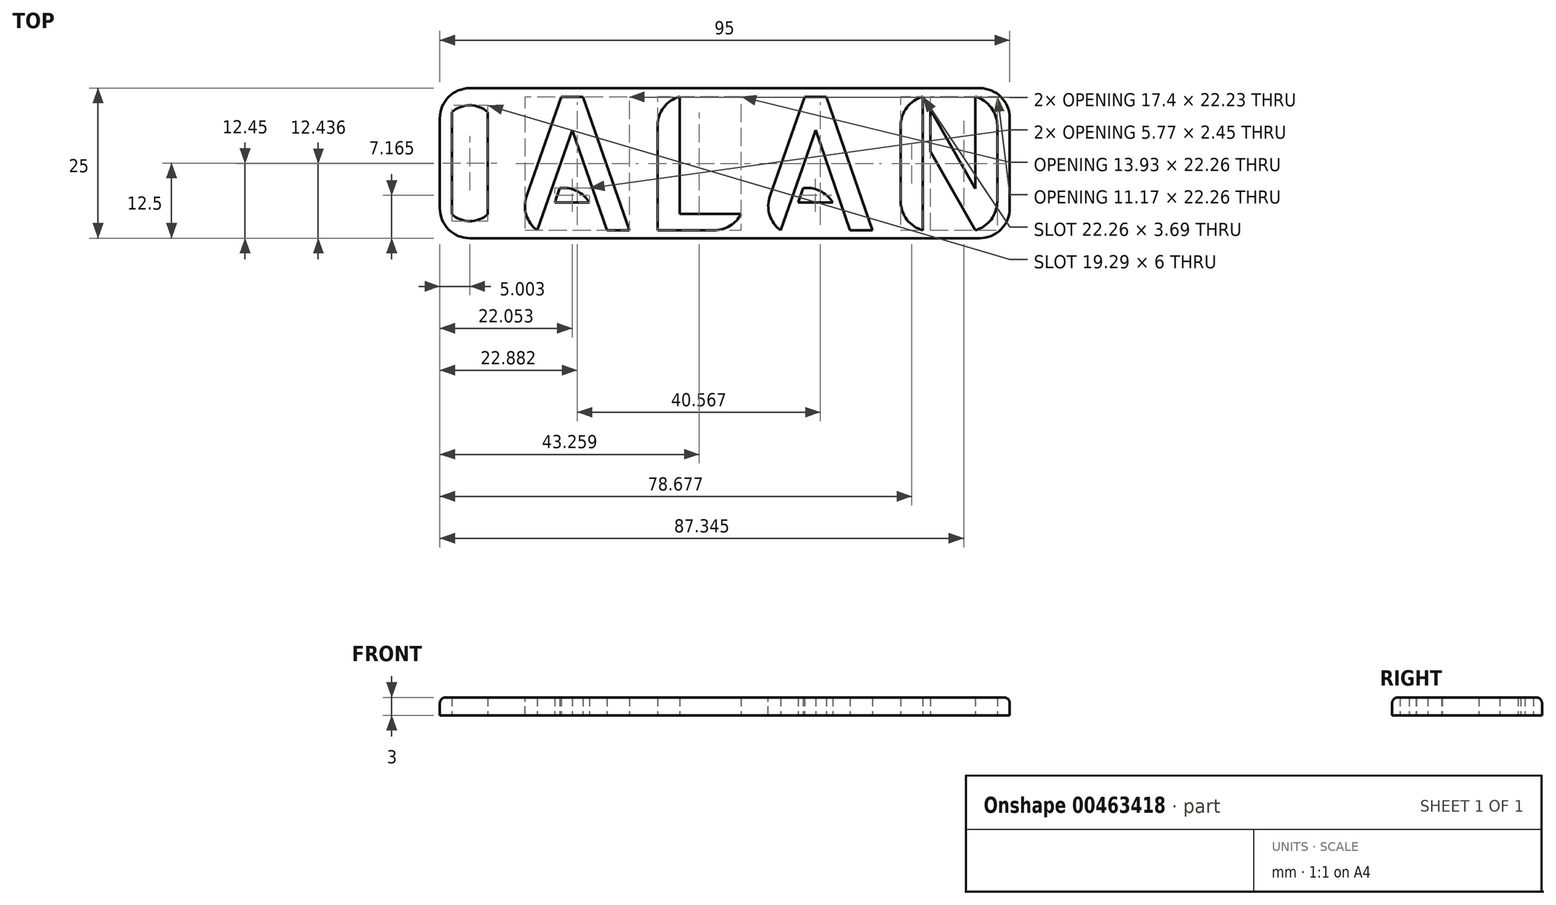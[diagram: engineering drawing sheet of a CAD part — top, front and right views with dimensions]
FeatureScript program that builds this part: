
annotation { "Feature Type Name" : "Feature", "Feature Type Description" : "" }
export const myFeature = defineFeature(function(context is Context, id is Id, definition is map)
    precondition{}
    {
        {
            var Q0;
            Q0=qCreatedBy(makeId("Top.planeOp"),FACE);
            var sketch = newSketch(context, id + "F0", { "sketchPlane" : qUnion([Q0])});
            skLineSegment(sketch, "E0.bottom", {"start": v(46.95, -25) * mm, "end": v(-48.05, -25) * mm});
            skLineSegment(sketch, "E0.top", {"start": v(46.95, 0) * mm, "end": v(-48.05, 0) * mm});
            skLineSegment(sketch, "E0.left", {"start": v(46.95, -25) * mm, "end": v(46.95, 0) * mm});
            skLineSegment(sketch, "E0.right", {"start": v(-48.05, -25) * mm, "end": v(-48.05, 0) * mm});
            skPoint(sketch, "E1.endSnap0", {"position": v(-48.05, -12.5) * mm});
            skText(sketch, "E2", { "text": "ALAN", "fontName": "AllertaStencil-Regular.ttf"});
            skArc(sketch, "E3", {"start": v(-40.05, -4) * mm, "mid": v(-43.05, -2.85) * mm, "end": v(-46.05, -4) * mm});
            skArc(sketch, "E4", {"start": v(-46.05, -21) * mm, "mid": v(-43.05, -22.15) * mm, "end": v(-40.05, -21) * mm});
            skLineSegment(sketch, "E5", {"start": v(-46.05, -4) * mm, "end": v(-46.05, -21) * mm});
            skLineSegment(sketch, "E6", {"start": v(-40.05, -4) * mm, "end": v(-40.05, -21) * mm});
            const initialGuessF0  = {"E2": [-0.03749, -0.02368, 1, 0, 0.02227]};
            skSetInitialGuess(sketch, initialGuessF0);
            skSolve(sketch);
        }
        {
            var Q0;
            Q0=makeQuery(id+"F0.imprint","IMPRINT",FACE,{"disambiguationData":[TD([[makeQuery(id+"F0.imprint","IMPRINT",EDGE,{"derivedFrom":sQuery(id+"F0.wireOp",EDGE,"E0.bottom")}),-1.0]])]});
            extrude(context, id + "F1", {"entities" : qUnion([Q0]), "depth" : 3 * mm});
        }
        {
            var Q0;
            Q0=makeQuery(id+"F1.opExtrude","SWEPT_EDGE",EDGE,{"disambiguationData":[OSD([sQuery(id+"F0.wireOp",EDGE,"E0.bottom"),sQuery(id+"F0.wireOp",EDGE,"E0.right")])]});
            var Q1;
            Q1=makeQuery(id+"F1.opExtrude","SWEPT_EDGE",EDGE,{"disambiguationData":[OSD([sQuery(id+"F0.wireOp",EDGE,"E0.top"),sQuery(id+"F0.wireOp",EDGE,"E0.right")])]});
            var Q2;
            Q2=makeQuery(id+"F1.opExtrude","SWEPT_EDGE",EDGE,{"disambiguationData":[OSD([sQuery(id+"F0.wireOp",EDGE,"E0.bottom"),sQuery(id+"F0.wireOp",EDGE,"E0.left")])]});
            var Q3;
            Q3=makeQuery(id+"F1.opExtrude","SWEPT_EDGE",EDGE,{"disambiguationData":[OSD([sQuery(id+"F0.wireOp",EDGE,"E0.top"),sQuery(id+"F0.wireOp",EDGE,"E0.left")])]});
            fillet(context, id + "F2", {"entities" : qUnion([Q0, Q1, Q2, Q3]), "radius" : 5 * mm, "tangentPropagation" : true, "allowEdgeOverflow" : false});
        }
        {
            var Q0;
            Q0=makeQuery(id+"F1.opExtrude","SWEPT_EDGE",EDGE,{"disambiguationData":[OSD([sQuery(id+"F0.wireOp",EDGE,"E2.sketch_text.stroke-28"),sQuery(id+"F0.wireOp",EDGE,"E2.sketch_text.stroke-29")])]});
            var Q1;
            Q1=makeQuery(id+"F1.opExtrude","SWEPT_EDGE",EDGE,{"disambiguationData":[OSD([sQuery(id+"F0.wireOp",EDGE,"E2.sketch_text.stroke-35"),sQuery(id+"F0.wireOp",EDGE,"E2.sketch_text.stroke-38")])]});
            var Q2;
            Q2=makeQuery(id+"F1.opExtrude","SWEPT_EDGE",EDGE,{"disambiguationData":[OSD([sQuery(id+"F0.wireOp",EDGE,"E2.sketch_text.stroke-35"),sQuery(id+"F0.wireOp",EDGE,"E2.sketch_text.stroke-36")])]});
            var Q3;
            Q3=makeQuery(id+"F1.opExtrude","SWEPT_EDGE",EDGE,{"disambiguationData":[OSD([sQuery(id+"F0.wireOp",EDGE,"E2.sketch_text.stroke-29"),sQuery(id+"F0.wireOp",EDGE,"E2.sketch_text.stroke-30")])]});
            var Q4;
            Q4=makeQuery(id+"F1.opExtrude","SWEPT_EDGE",EDGE,{"disambiguationData":[OSD([sQuery(id+"F0.wireOp",EDGE,"E2.sketch_text.stroke-20"),sQuery(id+"F0.wireOp",EDGE,"E2.sketch_text.stroke-21")])]});
            var Q5;
            Q5=makeQuery(id+"F1.opExtrude","SWEPT_EDGE",EDGE,{"disambiguationData":[OSD([sQuery(id+"F0.wireOp",EDGE,"E2.sketch_text.stroke-13"),sQuery(id+"F0.wireOp",EDGE,"E2.sketch_text.stroke-14")])]});
            var Q6;
            Q6=makeQuery(id+"F1.opExtrude","SWEPT_EDGE",EDGE,{"disambiguationData":[OSD([sQuery(id+"F0.wireOp",EDGE,"E2.sketch_text.stroke-15"),sQuery(id+"F0.wireOp",EDGE,"E2.sketch_text.stroke-16")])]});
            var Q7;
            Q7=makeQuery(id+"F1.opExtrude","SWEPT_EDGE",EDGE,{"disambiguationData":[OSD([sQuery(id+"F0.wireOp",EDGE,"E2.sketch_text.stroke-3"),sQuery(id+"F0.wireOp",EDGE,"E2.sketch_text.stroke-4")])]});
            var Q8;
            Q8=makeQuery(id+"F1.opExtrude","SWEPT_EDGE",EDGE,{"disambiguationData":[OSD([sQuery(id+"F0.wireOp",EDGE,"E2.sketch_text.stroke-7"),sQuery(id+"F0.wireOp",EDGE,"E2.sketch_text.stroke-10")])]});
            var Q9;
            Q9=makeQuery(id+"F1.opExtrude","SWEPT_EDGE",EDGE,{"disambiguationData":[OSD([sQuery(id+"F0.wireOp",EDGE,"E2.sketch_text.stroke-24"),sQuery(id+"F0.wireOp",EDGE,"E2.sketch_text.stroke-27")])]});
            fillet(context, id + "F3", {"entities" : qUnion([Q0, Q1, Q2, Q3, Q4, Q5, Q6, Q7, Q8, Q9]), "radius" : 5 * mm, "tangentPropagation" : true, "allowEdgeOverflow" : false});
        }
        {
            var Q0;
            Q0=makeQuery(id+"F1.opExtrude","CAP_EDGE",EDGE,{"disambiguationData":[OSD([sQuery(id+"F0.wireOp",EDGE,"E0.top")])],"isStart":false});
            var Q1;
            {var subQ0=sQuery(id+"F0.wireOp",EDGE,"E0.right");var subQ1=sQuery(id+"F0.wireOp",EDGE,"E0.top");Q1=makeQuery(id+"F2.opFillet","BLEND_EDGE",EDGE,{"blendedFrom":[makeQuery(id+"F1.opExtrude","SWEPT_EDGE",EDGE,{"disambiguationData":[OSD([subQ1,subQ0])]}),makeQuery(id+"F1.opExtrude","CAP_FACE",FACE,{"disambiguationData":[OSD([sQuery(id+"F0.wireOp",EDGE,"E0.bottom"),subQ1,sQuery(id+"F0.wireOp",EDGE,"E0.left"),subQ0,sQuery(id+"F0.wireOp",EDGE,"E2.sketch_text.stroke-0"),sQuery(id+"F0.wireOp",EDGE,"E2.sketch_text.stroke-1"),sQuery(id+"F0.wireOp",EDGE,"E2.sketch_text.stroke-2"),sQuery(id+"F0.wireOp",EDGE,"E2.sketch_text.stroke-3"),sQuery(id+"F0.wireOp",EDGE,"E2.sketch_text.stroke-4"),sQuery(id+"F0.wireOp",EDGE,"E2.sketch_text.stroke-5"),sQuery(id+"F0.wireOp",EDGE,"E2.sketch_text.stroke-6"),sQuery(id+"F0.wireOp",EDGE,"E2.sketch_text.stroke-7"),sQuery(id+"F0.wireOp",EDGE,"E2.sketch_text.stroke-8"),sQuery(id+"F0.wireOp",EDGE,"E2.sketch_text.stroke-9"),sQuery(id+"F0.wireOp",EDGE,"E2.sketch_text.stroke-10"),sQuery(id+"F0.wireOp",EDGE,"E2.sketch_text.stroke-11"),sQuery(id+"F0.wireOp",EDGE,"E2.sketch_text.stroke-12"),sQuery(id+"F0.wireOp",EDGE,"E2.sketch_text.stroke-13"),sQuery(id+"F0.wireOp",EDGE,"E2.sketch_text.stroke-14"),sQuery(id+"F0.wireOp",EDGE,"E2.sketch_text.stroke-15"),sQuery(id+"F0.wireOp",EDGE,"E2.sketch_text.stroke-16"),sQuery(id+"F0.wireOp",EDGE,"E2.sketch_text.stroke-17"),sQuery(id+"F0.wireOp",EDGE,"E2.sketch_text.stroke-18"),sQuery(id+"F0.wireOp",EDGE,"E2.sketch_text.stroke-19"),sQuery(id+"F0.wireOp",EDGE,"E2.sketch_text.stroke-20"),sQuery(id+"F0.wireOp",EDGE,"E2.sketch_text.stroke-21"),sQuery(id+"F0.wireOp",EDGE,"E2.sketch_text.stroke-22"),sQuery(id+"F0.wireOp",EDGE,"E2.sketch_text.stroke-23"),sQuery(id+"F0.wireOp",EDGE,"E2.sketch_text.stroke-24"),sQuery(id+"F0.wireOp",EDGE,"E2.sketch_text.stroke-25"),sQuery(id+"F0.wireOp",EDGE,"E2.sketch_text.stroke-26"),sQuery(id+"F0.wireOp",EDGE,"E2.sketch_text.stroke-27"),sQuery(id+"F0.wireOp",EDGE,"E2.sketch_text.stroke-28"),sQuery(id+"F0.wireOp",EDGE,"E2.sketch_text.stroke-29"),sQuery(id+"F0.wireOp",EDGE,"E2.sketch_text.stroke-30"),sQuery(id+"F0.wireOp",EDGE,"E2.sketch_text.stroke-31"),sQuery(id+"F0.wireOp",EDGE,"E2.sketch_text.stroke-32"),sQuery(id+"F0.wireOp",EDGE,"E2.sketch_text.stroke-33"),sQuery(id+"F0.wireOp",EDGE,"E2.sketch_text.stroke-34"),sQuery(id+"F0.wireOp",EDGE,"E2.sketch_text.stroke-35"),sQuery(id+"F0.wireOp",EDGE,"E2.sketch_text.stroke-36"),sQuery(id+"F0.wireOp",EDGE,"E2.sketch_text.stroke-37"),sQuery(id+"F0.wireOp",EDGE,"E2.sketch_text.stroke-38"),sQuery(id+"F0.wireOp",EDGE,"E3"),sQuery(id+"F0.wireOp",EDGE,"E4"),sQuery(id+"F0.wireOp",EDGE,"E5"),sQuery(id+"F0.wireOp",EDGE,"E6")])],"isStart":false})],"blendedInto":[makeQuery(id+"F1.opExtrude","CAP_FACE",FACE,{"disambiguationData":[OSD([sQuery(id+"F0.wireOp",EDGE,"E0.bottom"),subQ1,sQuery(id+"F0.wireOp",EDGE,"E0.left"),subQ0,sQuery(id+"F0.wireOp",EDGE,"E2.sketch_text.stroke-0"),sQuery(id+"F0.wireOp",EDGE,"E2.sketch_text.stroke-1"),sQuery(id+"F0.wireOp",EDGE,"E2.sketch_text.stroke-2"),sQuery(id+"F0.wireOp",EDGE,"E2.sketch_text.stroke-3"),sQuery(id+"F0.wireOp",EDGE,"E2.sketch_text.stroke-4"),sQuery(id+"F0.wireOp",EDGE,"E2.sketch_text.stroke-5"),sQuery(id+"F0.wireOp",EDGE,"E2.sketch_text.stroke-6"),sQuery(id+"F0.wireOp",EDGE,"E2.sketch_text.stroke-7"),sQuery(id+"F0.wireOp",EDGE,"E2.sketch_text.stroke-8"),sQuery(id+"F0.wireOp",EDGE,"E2.sketch_text.stroke-9"),sQuery(id+"F0.wireOp",EDGE,"E2.sketch_text.stroke-10"),sQuery(id+"F0.wireOp",EDGE,"E2.sketch_text.stroke-11"),sQuery(id+"F0.wireOp",EDGE,"E2.sketch_text.stroke-12"),sQuery(id+"F0.wireOp",EDGE,"E2.sketch_text.stroke-13"),sQuery(id+"F0.wireOp",EDGE,"E2.sketch_text.stroke-14"),sQuery(id+"F0.wireOp",EDGE,"E2.sketch_text.stroke-15"),sQuery(id+"F0.wireOp",EDGE,"E2.sketch_text.stroke-16"),sQuery(id+"F0.wireOp",EDGE,"E2.sketch_text.stroke-17"),sQuery(id+"F0.wireOp",EDGE,"E2.sketch_text.stroke-18"),sQuery(id+"F0.wireOp",EDGE,"E2.sketch_text.stroke-19"),sQuery(id+"F0.wireOp",EDGE,"E2.sketch_text.stroke-20"),sQuery(id+"F0.wireOp",EDGE,"E2.sketch_text.stroke-21"),sQuery(id+"F0.wireOp",EDGE,"E2.sketch_text.stroke-22"),sQuery(id+"F0.wireOp",EDGE,"E2.sketch_text.stroke-23"),sQuery(id+"F0.wireOp",EDGE,"E2.sketch_text.stroke-24"),sQuery(id+"F0.wireOp",EDGE,"E2.sketch_text.stroke-25"),sQuery(id+"F0.wireOp",EDGE,"E2.sketch_text.stroke-26"),sQuery(id+"F0.wireOp",EDGE,"E2.sketch_text.stroke-27"),sQuery(id+"F0.wireOp",EDGE,"E2.sketch_text.stroke-28"),sQuery(id+"F0.wireOp",EDGE,"E2.sketch_text.stroke-29"),sQuery(id+"F0.wireOp",EDGE,"E2.sketch_text.stroke-30"),sQuery(id+"F0.wireOp",EDGE,"E2.sketch_text.stroke-31"),sQuery(id+"F0.wireOp",EDGE,"E2.sketch_text.stroke-32"),sQuery(id+"F0.wireOp",EDGE,"E2.sketch_text.stroke-33"),sQuery(id+"F0.wireOp",EDGE,"E2.sketch_text.stroke-34"),sQuery(id+"F0.wireOp",EDGE,"E2.sketch_text.stroke-35"),sQuery(id+"F0.wireOp",EDGE,"E2.sketch_text.stroke-36"),sQuery(id+"F0.wireOp",EDGE,"E2.sketch_text.stroke-37"),sQuery(id+"F0.wireOp",EDGE,"E2.sketch_text.stroke-38"),sQuery(id+"F0.wireOp",EDGE,"E3"),sQuery(id+"F0.wireOp",EDGE,"E4"),sQuery(id+"F0.wireOp",EDGE,"E5"),sQuery(id+"F0.wireOp",EDGE,"E6")])],"isStart":false})]});}
            var Q2;
            Q2=makeQuery(id+"F1.opExtrude","CAP_EDGE",EDGE,{"disambiguationData":[OSD([sQuery(id+"F0.wireOp",EDGE,"E0.right")])],"isStart":false});
            var Q3;
            {var subQ0=sQuery(id+"F0.wireOp",EDGE,"E0.right");var subQ1=sQuery(id+"F0.wireOp",EDGE,"E0.bottom");Q3=makeQuery(id+"F2.opFillet","BLEND_EDGE",EDGE,{"blendedFrom":[makeQuery(id+"F1.opExtrude","SWEPT_EDGE",EDGE,{"disambiguationData":[OSD([subQ1,subQ0])]}),makeQuery(id+"F1.opExtrude","CAP_FACE",FACE,{"disambiguationData":[OSD([subQ1,sQuery(id+"F0.wireOp",EDGE,"E0.top"),sQuery(id+"F0.wireOp",EDGE,"E0.left"),subQ0,sQuery(id+"F0.wireOp",EDGE,"E2.sketch_text.stroke-0"),sQuery(id+"F0.wireOp",EDGE,"E2.sketch_text.stroke-1"),sQuery(id+"F0.wireOp",EDGE,"E2.sketch_text.stroke-2"),sQuery(id+"F0.wireOp",EDGE,"E2.sketch_text.stroke-3"),sQuery(id+"F0.wireOp",EDGE,"E2.sketch_text.stroke-4"),sQuery(id+"F0.wireOp",EDGE,"E2.sketch_text.stroke-5"),sQuery(id+"F0.wireOp",EDGE,"E2.sketch_text.stroke-6"),sQuery(id+"F0.wireOp",EDGE,"E2.sketch_text.stroke-7"),sQuery(id+"F0.wireOp",EDGE,"E2.sketch_text.stroke-8"),sQuery(id+"F0.wireOp",EDGE,"E2.sketch_text.stroke-9"),sQuery(id+"F0.wireOp",EDGE,"E2.sketch_text.stroke-10"),sQuery(id+"F0.wireOp",EDGE,"E2.sketch_text.stroke-11"),sQuery(id+"F0.wireOp",EDGE,"E2.sketch_text.stroke-12"),sQuery(id+"F0.wireOp",EDGE,"E2.sketch_text.stroke-13"),sQuery(id+"F0.wireOp",EDGE,"E2.sketch_text.stroke-14"),sQuery(id+"F0.wireOp",EDGE,"E2.sketch_text.stroke-15"),sQuery(id+"F0.wireOp",EDGE,"E2.sketch_text.stroke-16"),sQuery(id+"F0.wireOp",EDGE,"E2.sketch_text.stroke-17"),sQuery(id+"F0.wireOp",EDGE,"E2.sketch_text.stroke-18"),sQuery(id+"F0.wireOp",EDGE,"E2.sketch_text.stroke-19"),sQuery(id+"F0.wireOp",EDGE,"E2.sketch_text.stroke-20"),sQuery(id+"F0.wireOp",EDGE,"E2.sketch_text.stroke-21"),sQuery(id+"F0.wireOp",EDGE,"E2.sketch_text.stroke-22"),sQuery(id+"F0.wireOp",EDGE,"E2.sketch_text.stroke-23"),sQuery(id+"F0.wireOp",EDGE,"E2.sketch_text.stroke-24"),sQuery(id+"F0.wireOp",EDGE,"E2.sketch_text.stroke-25"),sQuery(id+"F0.wireOp",EDGE,"E2.sketch_text.stroke-26"),sQuery(id+"F0.wireOp",EDGE,"E2.sketch_text.stroke-27"),sQuery(id+"F0.wireOp",EDGE,"E2.sketch_text.stroke-28"),sQuery(id+"F0.wireOp",EDGE,"E2.sketch_text.stroke-29"),sQuery(id+"F0.wireOp",EDGE,"E2.sketch_text.stroke-30"),sQuery(id+"F0.wireOp",EDGE,"E2.sketch_text.stroke-31"),sQuery(id+"F0.wireOp",EDGE,"E2.sketch_text.stroke-32"),sQuery(id+"F0.wireOp",EDGE,"E2.sketch_text.stroke-33"),sQuery(id+"F0.wireOp",EDGE,"E2.sketch_text.stroke-34"),sQuery(id+"F0.wireOp",EDGE,"E2.sketch_text.stroke-35"),sQuery(id+"F0.wireOp",EDGE,"E2.sketch_text.stroke-36"),sQuery(id+"F0.wireOp",EDGE,"E2.sketch_text.stroke-37"),sQuery(id+"F0.wireOp",EDGE,"E2.sketch_text.stroke-38"),sQuery(id+"F0.wireOp",EDGE,"E3"),sQuery(id+"F0.wireOp",EDGE,"E4"),sQuery(id+"F0.wireOp",EDGE,"E5"),sQuery(id+"F0.wireOp",EDGE,"E6")])],"isStart":false})],"blendedInto":[makeQuery(id+"F1.opExtrude","CAP_FACE",FACE,{"disambiguationData":[OSD([subQ1,sQuery(id+"F0.wireOp",EDGE,"E0.top"),sQuery(id+"F0.wireOp",EDGE,"E0.left"),subQ0,sQuery(id+"F0.wireOp",EDGE,"E2.sketch_text.stroke-0"),sQuery(id+"F0.wireOp",EDGE,"E2.sketch_text.stroke-1"),sQuery(id+"F0.wireOp",EDGE,"E2.sketch_text.stroke-2"),sQuery(id+"F0.wireOp",EDGE,"E2.sketch_text.stroke-3"),sQuery(id+"F0.wireOp",EDGE,"E2.sketch_text.stroke-4"),sQuery(id+"F0.wireOp",EDGE,"E2.sketch_text.stroke-5"),sQuery(id+"F0.wireOp",EDGE,"E2.sketch_text.stroke-6"),sQuery(id+"F0.wireOp",EDGE,"E2.sketch_text.stroke-7"),sQuery(id+"F0.wireOp",EDGE,"E2.sketch_text.stroke-8"),sQuery(id+"F0.wireOp",EDGE,"E2.sketch_text.stroke-9"),sQuery(id+"F0.wireOp",EDGE,"E2.sketch_text.stroke-10"),sQuery(id+"F0.wireOp",EDGE,"E2.sketch_text.stroke-11"),sQuery(id+"F0.wireOp",EDGE,"E2.sketch_text.stroke-12"),sQuery(id+"F0.wireOp",EDGE,"E2.sketch_text.stroke-13"),sQuery(id+"F0.wireOp",EDGE,"E2.sketch_text.stroke-14"),sQuery(id+"F0.wireOp",EDGE,"E2.sketch_text.stroke-15"),sQuery(id+"F0.wireOp",EDGE,"E2.sketch_text.stroke-16"),sQuery(id+"F0.wireOp",EDGE,"E2.sketch_text.stroke-17"),sQuery(id+"F0.wireOp",EDGE,"E2.sketch_text.stroke-18"),sQuery(id+"F0.wireOp",EDGE,"E2.sketch_text.stroke-19"),sQuery(id+"F0.wireOp",EDGE,"E2.sketch_text.stroke-20"),sQuery(id+"F0.wireOp",EDGE,"E2.sketch_text.stroke-21"),sQuery(id+"F0.wireOp",EDGE,"E2.sketch_text.stroke-22"),sQuery(id+"F0.wireOp",EDGE,"E2.sketch_text.stroke-23"),sQuery(id+"F0.wireOp",EDGE,"E2.sketch_text.stroke-24"),sQuery(id+"F0.wireOp",EDGE,"E2.sketch_text.stroke-25"),sQuery(id+"F0.wireOp",EDGE,"E2.sketch_text.stroke-26"),sQuery(id+"F0.wireOp",EDGE,"E2.sketch_text.stroke-27"),sQuery(id+"F0.wireOp",EDGE,"E2.sketch_text.stroke-28"),sQuery(id+"F0.wireOp",EDGE,"E2.sketch_text.stroke-29"),sQuery(id+"F0.wireOp",EDGE,"E2.sketch_text.stroke-30"),sQuery(id+"F0.wireOp",EDGE,"E2.sketch_text.stroke-31"),sQuery(id+"F0.wireOp",EDGE,"E2.sketch_text.stroke-32"),sQuery(id+"F0.wireOp",EDGE,"E2.sketch_text.stroke-33"),sQuery(id+"F0.wireOp",EDGE,"E2.sketch_text.stroke-34"),sQuery(id+"F0.wireOp",EDGE,"E2.sketch_text.stroke-35"),sQuery(id+"F0.wireOp",EDGE,"E2.sketch_text.stroke-36"),sQuery(id+"F0.wireOp",EDGE,"E2.sketch_text.stroke-37"),sQuery(id+"F0.wireOp",EDGE,"E2.sketch_text.stroke-38"),sQuery(id+"F0.wireOp",EDGE,"E3"),sQuery(id+"F0.wireOp",EDGE,"E4"),sQuery(id+"F0.wireOp",EDGE,"E5"),sQuery(id+"F0.wireOp",EDGE,"E6")])],"isStart":false})]});}
            var Q4;
            Q4=makeQuery(id+"F1.opExtrude","CAP_EDGE",EDGE,{"disambiguationData":[OSD([sQuery(id+"F0.wireOp",EDGE,"E0.bottom")])],"isStart":false});
            var Q5;
            {var subQ0=sQuery(id+"F0.wireOp",EDGE,"E0.left");var subQ1=sQuery(id+"F0.wireOp",EDGE,"E0.bottom");Q5=makeQuery(id+"F2.opFillet","BLEND_EDGE",EDGE,{"blendedFrom":[makeQuery(id+"F1.opExtrude","SWEPT_EDGE",EDGE,{"disambiguationData":[OSD([subQ1,subQ0])]}),makeQuery(id+"F1.opExtrude","CAP_FACE",FACE,{"disambiguationData":[OSD([subQ1,sQuery(id+"F0.wireOp",EDGE,"E0.top"),subQ0,sQuery(id+"F0.wireOp",EDGE,"E0.right"),sQuery(id+"F0.wireOp",EDGE,"E2.sketch_text.stroke-0"),sQuery(id+"F0.wireOp",EDGE,"E2.sketch_text.stroke-1"),sQuery(id+"F0.wireOp",EDGE,"E2.sketch_text.stroke-2"),sQuery(id+"F0.wireOp",EDGE,"E2.sketch_text.stroke-3"),sQuery(id+"F0.wireOp",EDGE,"E2.sketch_text.stroke-4"),sQuery(id+"F0.wireOp",EDGE,"E2.sketch_text.stroke-5"),sQuery(id+"F0.wireOp",EDGE,"E2.sketch_text.stroke-6"),sQuery(id+"F0.wireOp",EDGE,"E2.sketch_text.stroke-7"),sQuery(id+"F0.wireOp",EDGE,"E2.sketch_text.stroke-8"),sQuery(id+"F0.wireOp",EDGE,"E2.sketch_text.stroke-9"),sQuery(id+"F0.wireOp",EDGE,"E2.sketch_text.stroke-10"),sQuery(id+"F0.wireOp",EDGE,"E2.sketch_text.stroke-11"),sQuery(id+"F0.wireOp",EDGE,"E2.sketch_text.stroke-12"),sQuery(id+"F0.wireOp",EDGE,"E2.sketch_text.stroke-13"),sQuery(id+"F0.wireOp",EDGE,"E2.sketch_text.stroke-14"),sQuery(id+"F0.wireOp",EDGE,"E2.sketch_text.stroke-15"),sQuery(id+"F0.wireOp",EDGE,"E2.sketch_text.stroke-16"),sQuery(id+"F0.wireOp",EDGE,"E2.sketch_text.stroke-17"),sQuery(id+"F0.wireOp",EDGE,"E2.sketch_text.stroke-18"),sQuery(id+"F0.wireOp",EDGE,"E2.sketch_text.stroke-19"),sQuery(id+"F0.wireOp",EDGE,"E2.sketch_text.stroke-20"),sQuery(id+"F0.wireOp",EDGE,"E2.sketch_text.stroke-21"),sQuery(id+"F0.wireOp",EDGE,"E2.sketch_text.stroke-22"),sQuery(id+"F0.wireOp",EDGE,"E2.sketch_text.stroke-23"),sQuery(id+"F0.wireOp",EDGE,"E2.sketch_text.stroke-24"),sQuery(id+"F0.wireOp",EDGE,"E2.sketch_text.stroke-25"),sQuery(id+"F0.wireOp",EDGE,"E2.sketch_text.stroke-26"),sQuery(id+"F0.wireOp",EDGE,"E2.sketch_text.stroke-27"),sQuery(id+"F0.wireOp",EDGE,"E2.sketch_text.stroke-28"),sQuery(id+"F0.wireOp",EDGE,"E2.sketch_text.stroke-29"),sQuery(id+"F0.wireOp",EDGE,"E2.sketch_text.stroke-30"),sQuery(id+"F0.wireOp",EDGE,"E2.sketch_text.stroke-31"),sQuery(id+"F0.wireOp",EDGE,"E2.sketch_text.stroke-32"),sQuery(id+"F0.wireOp",EDGE,"E2.sketch_text.stroke-33"),sQuery(id+"F0.wireOp",EDGE,"E2.sketch_text.stroke-34"),sQuery(id+"F0.wireOp",EDGE,"E2.sketch_text.stroke-35"),sQuery(id+"F0.wireOp",EDGE,"E2.sketch_text.stroke-36"),sQuery(id+"F0.wireOp",EDGE,"E2.sketch_text.stroke-37"),sQuery(id+"F0.wireOp",EDGE,"E2.sketch_text.stroke-38"),sQuery(id+"F0.wireOp",EDGE,"E3"),sQuery(id+"F0.wireOp",EDGE,"E4"),sQuery(id+"F0.wireOp",EDGE,"E5"),sQuery(id+"F0.wireOp",EDGE,"E6")])],"isStart":false})],"blendedInto":[makeQuery(id+"F1.opExtrude","CAP_FACE",FACE,{"disambiguationData":[OSD([subQ1,sQuery(id+"F0.wireOp",EDGE,"E0.top"),subQ0,sQuery(id+"F0.wireOp",EDGE,"E0.right"),sQuery(id+"F0.wireOp",EDGE,"E2.sketch_text.stroke-0"),sQuery(id+"F0.wireOp",EDGE,"E2.sketch_text.stroke-1"),sQuery(id+"F0.wireOp",EDGE,"E2.sketch_text.stroke-2"),sQuery(id+"F0.wireOp",EDGE,"E2.sketch_text.stroke-3"),sQuery(id+"F0.wireOp",EDGE,"E2.sketch_text.stroke-4"),sQuery(id+"F0.wireOp",EDGE,"E2.sketch_text.stroke-5"),sQuery(id+"F0.wireOp",EDGE,"E2.sketch_text.stroke-6"),sQuery(id+"F0.wireOp",EDGE,"E2.sketch_text.stroke-7"),sQuery(id+"F0.wireOp",EDGE,"E2.sketch_text.stroke-8"),sQuery(id+"F0.wireOp",EDGE,"E2.sketch_text.stroke-9"),sQuery(id+"F0.wireOp",EDGE,"E2.sketch_text.stroke-10"),sQuery(id+"F0.wireOp",EDGE,"E2.sketch_text.stroke-11"),sQuery(id+"F0.wireOp",EDGE,"E2.sketch_text.stroke-12"),sQuery(id+"F0.wireOp",EDGE,"E2.sketch_text.stroke-13"),sQuery(id+"F0.wireOp",EDGE,"E2.sketch_text.stroke-14"),sQuery(id+"F0.wireOp",EDGE,"E2.sketch_text.stroke-15"),sQuery(id+"F0.wireOp",EDGE,"E2.sketch_text.stroke-16"),sQuery(id+"F0.wireOp",EDGE,"E2.sketch_text.stroke-17"),sQuery(id+"F0.wireOp",EDGE,"E2.sketch_text.stroke-18"),sQuery(id+"F0.wireOp",EDGE,"E2.sketch_text.stroke-19"),sQuery(id+"F0.wireOp",EDGE,"E2.sketch_text.stroke-20"),sQuery(id+"F0.wireOp",EDGE,"E2.sketch_text.stroke-21"),sQuery(id+"F0.wireOp",EDGE,"E2.sketch_text.stroke-22"),sQuery(id+"F0.wireOp",EDGE,"E2.sketch_text.stroke-23"),sQuery(id+"F0.wireOp",EDGE,"E2.sketch_text.stroke-24"),sQuery(id+"F0.wireOp",EDGE,"E2.sketch_text.stroke-25"),sQuery(id+"F0.wireOp",EDGE,"E2.sketch_text.stroke-26"),sQuery(id+"F0.wireOp",EDGE,"E2.sketch_text.stroke-27"),sQuery(id+"F0.wireOp",EDGE,"E2.sketch_text.stroke-28"),sQuery(id+"F0.wireOp",EDGE,"E2.sketch_text.stroke-29"),sQuery(id+"F0.wireOp",EDGE,"E2.sketch_text.stroke-30"),sQuery(id+"F0.wireOp",EDGE,"E2.sketch_text.stroke-31"),sQuery(id+"F0.wireOp",EDGE,"E2.sketch_text.stroke-32"),sQuery(id+"F0.wireOp",EDGE,"E2.sketch_text.stroke-33"),sQuery(id+"F0.wireOp",EDGE,"E2.sketch_text.stroke-34"),sQuery(id+"F0.wireOp",EDGE,"E2.sketch_text.stroke-35"),sQuery(id+"F0.wireOp",EDGE,"E2.sketch_text.stroke-36"),sQuery(id+"F0.wireOp",EDGE,"E2.sketch_text.stroke-37"),sQuery(id+"F0.wireOp",EDGE,"E2.sketch_text.stroke-38"),sQuery(id+"F0.wireOp",EDGE,"E3"),sQuery(id+"F0.wireOp",EDGE,"E4"),sQuery(id+"F0.wireOp",EDGE,"E5"),sQuery(id+"F0.wireOp",EDGE,"E6")])],"isStart":false})]});}
            var Q6;
            Q6=makeQuery(id+"F1.opExtrude","CAP_EDGE",EDGE,{"disambiguationData":[OSD([sQuery(id+"F0.wireOp",EDGE,"E0.left")])],"isStart":false});
            var Q7;
            {var subQ0=sQuery(id+"F0.wireOp",EDGE,"E0.left");var subQ1=sQuery(id+"F0.wireOp",EDGE,"E0.top");Q7=makeQuery(id+"F2.opFillet","BLEND_EDGE",EDGE,{"blendedFrom":[makeQuery(id+"F1.opExtrude","SWEPT_EDGE",EDGE,{"disambiguationData":[OSD([subQ1,subQ0])]}),makeQuery(id+"F1.opExtrude","CAP_FACE",FACE,{"disambiguationData":[OSD([sQuery(id+"F0.wireOp",EDGE,"E0.bottom"),subQ1,subQ0,sQuery(id+"F0.wireOp",EDGE,"E0.right"),sQuery(id+"F0.wireOp",EDGE,"E2.sketch_text.stroke-0"),sQuery(id+"F0.wireOp",EDGE,"E2.sketch_text.stroke-1"),sQuery(id+"F0.wireOp",EDGE,"E2.sketch_text.stroke-2"),sQuery(id+"F0.wireOp",EDGE,"E2.sketch_text.stroke-3"),sQuery(id+"F0.wireOp",EDGE,"E2.sketch_text.stroke-4"),sQuery(id+"F0.wireOp",EDGE,"E2.sketch_text.stroke-5"),sQuery(id+"F0.wireOp",EDGE,"E2.sketch_text.stroke-6"),sQuery(id+"F0.wireOp",EDGE,"E2.sketch_text.stroke-7"),sQuery(id+"F0.wireOp",EDGE,"E2.sketch_text.stroke-8"),sQuery(id+"F0.wireOp",EDGE,"E2.sketch_text.stroke-9"),sQuery(id+"F0.wireOp",EDGE,"E2.sketch_text.stroke-10"),sQuery(id+"F0.wireOp",EDGE,"E2.sketch_text.stroke-11"),sQuery(id+"F0.wireOp",EDGE,"E2.sketch_text.stroke-12"),sQuery(id+"F0.wireOp",EDGE,"E2.sketch_text.stroke-13"),sQuery(id+"F0.wireOp",EDGE,"E2.sketch_text.stroke-14"),sQuery(id+"F0.wireOp",EDGE,"E2.sketch_text.stroke-15"),sQuery(id+"F0.wireOp",EDGE,"E2.sketch_text.stroke-16"),sQuery(id+"F0.wireOp",EDGE,"E2.sketch_text.stroke-17"),sQuery(id+"F0.wireOp",EDGE,"E2.sketch_text.stroke-18"),sQuery(id+"F0.wireOp",EDGE,"E2.sketch_text.stroke-19"),sQuery(id+"F0.wireOp",EDGE,"E2.sketch_text.stroke-20"),sQuery(id+"F0.wireOp",EDGE,"E2.sketch_text.stroke-21"),sQuery(id+"F0.wireOp",EDGE,"E2.sketch_text.stroke-22"),sQuery(id+"F0.wireOp",EDGE,"E2.sketch_text.stroke-23"),sQuery(id+"F0.wireOp",EDGE,"E2.sketch_text.stroke-24"),sQuery(id+"F0.wireOp",EDGE,"E2.sketch_text.stroke-25"),sQuery(id+"F0.wireOp",EDGE,"E2.sketch_text.stroke-26"),sQuery(id+"F0.wireOp",EDGE,"E2.sketch_text.stroke-27"),sQuery(id+"F0.wireOp",EDGE,"E2.sketch_text.stroke-28"),sQuery(id+"F0.wireOp",EDGE,"E2.sketch_text.stroke-29"),sQuery(id+"F0.wireOp",EDGE,"E2.sketch_text.stroke-30"),sQuery(id+"F0.wireOp",EDGE,"E2.sketch_text.stroke-31"),sQuery(id+"F0.wireOp",EDGE,"E2.sketch_text.stroke-32"),sQuery(id+"F0.wireOp",EDGE,"E2.sketch_text.stroke-33"),sQuery(id+"F0.wireOp",EDGE,"E2.sketch_text.stroke-34"),sQuery(id+"F0.wireOp",EDGE,"E2.sketch_text.stroke-35"),sQuery(id+"F0.wireOp",EDGE,"E2.sketch_text.stroke-36"),sQuery(id+"F0.wireOp",EDGE,"E2.sketch_text.stroke-37"),sQuery(id+"F0.wireOp",EDGE,"E2.sketch_text.stroke-38"),sQuery(id+"F0.wireOp",EDGE,"E3"),sQuery(id+"F0.wireOp",EDGE,"E4"),sQuery(id+"F0.wireOp",EDGE,"E5"),sQuery(id+"F0.wireOp",EDGE,"E6")])],"isStart":false})],"blendedInto":[makeQuery(id+"F1.opExtrude","CAP_FACE",FACE,{"disambiguationData":[OSD([sQuery(id+"F0.wireOp",EDGE,"E0.bottom"),subQ1,subQ0,sQuery(id+"F0.wireOp",EDGE,"E0.right"),sQuery(id+"F0.wireOp",EDGE,"E2.sketch_text.stroke-0"),sQuery(id+"F0.wireOp",EDGE,"E2.sketch_text.stroke-1"),sQuery(id+"F0.wireOp",EDGE,"E2.sketch_text.stroke-2"),sQuery(id+"F0.wireOp",EDGE,"E2.sketch_text.stroke-3"),sQuery(id+"F0.wireOp",EDGE,"E2.sketch_text.stroke-4"),sQuery(id+"F0.wireOp",EDGE,"E2.sketch_text.stroke-5"),sQuery(id+"F0.wireOp",EDGE,"E2.sketch_text.stroke-6"),sQuery(id+"F0.wireOp",EDGE,"E2.sketch_text.stroke-7"),sQuery(id+"F0.wireOp",EDGE,"E2.sketch_text.stroke-8"),sQuery(id+"F0.wireOp",EDGE,"E2.sketch_text.stroke-9"),sQuery(id+"F0.wireOp",EDGE,"E2.sketch_text.stroke-10"),sQuery(id+"F0.wireOp",EDGE,"E2.sketch_text.stroke-11"),sQuery(id+"F0.wireOp",EDGE,"E2.sketch_text.stroke-12"),sQuery(id+"F0.wireOp",EDGE,"E2.sketch_text.stroke-13"),sQuery(id+"F0.wireOp",EDGE,"E2.sketch_text.stroke-14"),sQuery(id+"F0.wireOp",EDGE,"E2.sketch_text.stroke-15"),sQuery(id+"F0.wireOp",EDGE,"E2.sketch_text.stroke-16"),sQuery(id+"F0.wireOp",EDGE,"E2.sketch_text.stroke-17"),sQuery(id+"F0.wireOp",EDGE,"E2.sketch_text.stroke-18"),sQuery(id+"F0.wireOp",EDGE,"E2.sketch_text.stroke-19"),sQuery(id+"F0.wireOp",EDGE,"E2.sketch_text.stroke-20"),sQuery(id+"F0.wireOp",EDGE,"E2.sketch_text.stroke-21"),sQuery(id+"F0.wireOp",EDGE,"E2.sketch_text.stroke-22"),sQuery(id+"F0.wireOp",EDGE,"E2.sketch_text.stroke-23"),sQuery(id+"F0.wireOp",EDGE,"E2.sketch_text.stroke-24"),sQuery(id+"F0.wireOp",EDGE,"E2.sketch_text.stroke-25"),sQuery(id+"F0.wireOp",EDGE,"E2.sketch_text.stroke-26"),sQuery(id+"F0.wireOp",EDGE,"E2.sketch_text.stroke-27"),sQuery(id+"F0.wireOp",EDGE,"E2.sketch_text.stroke-28"),sQuery(id+"F0.wireOp",EDGE,"E2.sketch_text.stroke-29"),sQuery(id+"F0.wireOp",EDGE,"E2.sketch_text.stroke-30"),sQuery(id+"F0.wireOp",EDGE,"E2.sketch_text.stroke-31"),sQuery(id+"F0.wireOp",EDGE,"E2.sketch_text.stroke-32"),sQuery(id+"F0.wireOp",EDGE,"E2.sketch_text.stroke-33"),sQuery(id+"F0.wireOp",EDGE,"E2.sketch_text.stroke-34"),sQuery(id+"F0.wireOp",EDGE,"E2.sketch_text.stroke-35"),sQuery(id+"F0.wireOp",EDGE,"E2.sketch_text.stroke-36"),sQuery(id+"F0.wireOp",EDGE,"E2.sketch_text.stroke-37"),sQuery(id+"F0.wireOp",EDGE,"E2.sketch_text.stroke-38"),sQuery(id+"F0.wireOp",EDGE,"E3"),sQuery(id+"F0.wireOp",EDGE,"E4"),sQuery(id+"F0.wireOp",EDGE,"E5"),sQuery(id+"F0.wireOp",EDGE,"E6")])],"isStart":false})]});}
            fillet(context, id + "F4", {"entities" : qUnion([Q0, Q1, Q2, Q3, Q4, Q5, Q6, Q7]), "radius" : 1 * mm, "tangentPropagation" : true, "allowEdgeOverflow" : false});
        }
    });
